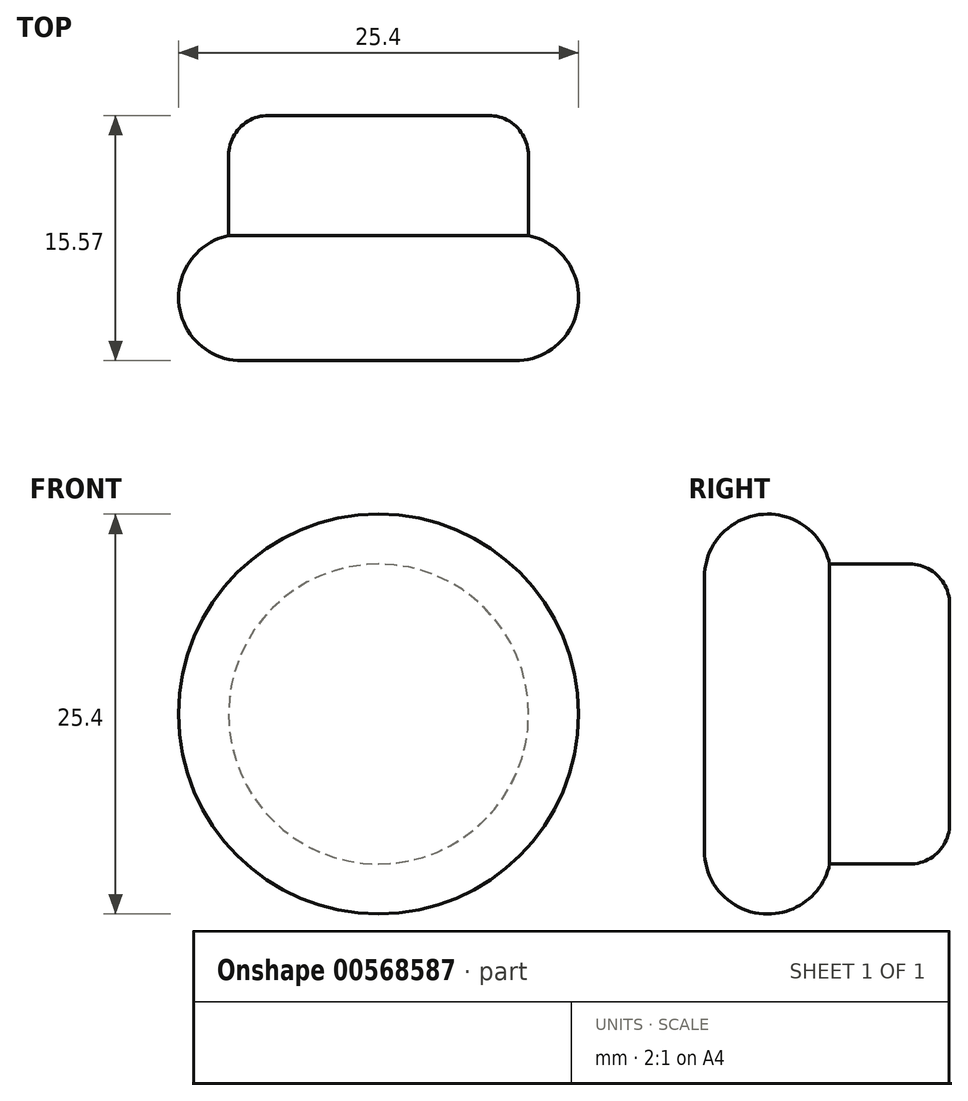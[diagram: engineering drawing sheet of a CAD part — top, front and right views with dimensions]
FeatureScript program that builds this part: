
annotation { "Feature Type Name" : "Feature", "Feature Type Description" : "" }
export const myFeature = defineFeature(function(context is Context, id is Id, definition is map)
    precondition{}
    {
        {
            var Q0;
            Q0=qCreatedBy(makeId("Front.planeOp"),FACE);
            var sketch = newSketch(context, id + "F0", { "sketchPlane" : qUnion([Q0])});
            skCircle(sketch, "E0", {"center": v(0, 0) * mm, "radius": 9.53 * mm});
            skSolve(sketch);
        }
        {
            var Q0;
            Q0=makeQuery(id+"F0.imprint","IMPRINT",FACE,{"disambiguationData":[TD([[makeQuery(id+"F0.imprint","IMPRINT",EDGE,{"derivedFrom":sQuery(id+"F0.wireOp",EDGE,"E0")}),1.0]])]});
            extrude(context, id + "F1", {"entities" : qUnion([Q0]), "depth" : 7.62 * mm, "offsetDistance" : 25.4 * mm});
        }
        {
            var Q0;
            Q0=makeQuery(id+"F1.opExtrude","CAP_FACE",FACE,{"disambiguationData":[OSD([sQuery(id+"F0.wireOp",EDGE,"E0")])],"isStart":false});
            var sketch = newSketch(context, id + "F2", { "sketchPlane" : qUnion([Q0])});
            skCircle(sketch, "E1", {"center": v(0, 0) * mm, "radius": 12.7 * mm});
            skSolve(sketch);
        }
        {
            var Q0;
            Q0 = qSketchRegion(id + "F2", true);
            extrude(context, id + "F3", {"entities" : qUnion([Q0]), "operationType" : NewBodyOperationType.ADD, "depth" : 7.95 * mm, "offsetDistance" : 25.4 * mm});
        }
        {
            var Q0;
            Q0=makeQuery(id+"F3.opExtrude","CAP_EDGE",EDGE,{"disambiguationData":[OSD([sQuery(id+"F2.wireOp",EDGE,"E1")])],"isStart":false});
            var Q1;
            Q1=makeQuery(id+"F3.opExtrude","CAP_EDGE",EDGE,{"disambiguationData":[OSD([sQuery(id+"F2.wireOp",EDGE,"E1")])],"isStart":true});
            fillet(context, id + "F4", {"entities" : qUnion([Q0, Q1]), "radius" : 4 * mm, "tangentPropagation" : true, "allowEdgeOverflow" : false});
        }
        {
            var Q0;
            Q0=makeQuery(id+"F1.opExtrude","CAP_EDGE",EDGE,{"disambiguationData":[OSD([sQuery(id+"F0.wireOp",EDGE,"E0")])],"isStart":true});
            fillet(context, id + "F5", {"entities" : qUnion([Q0]), "radius" : 2.54 * mm, "tangentPropagation" : true, "allowEdgeOverflow" : false});
        }
    });
